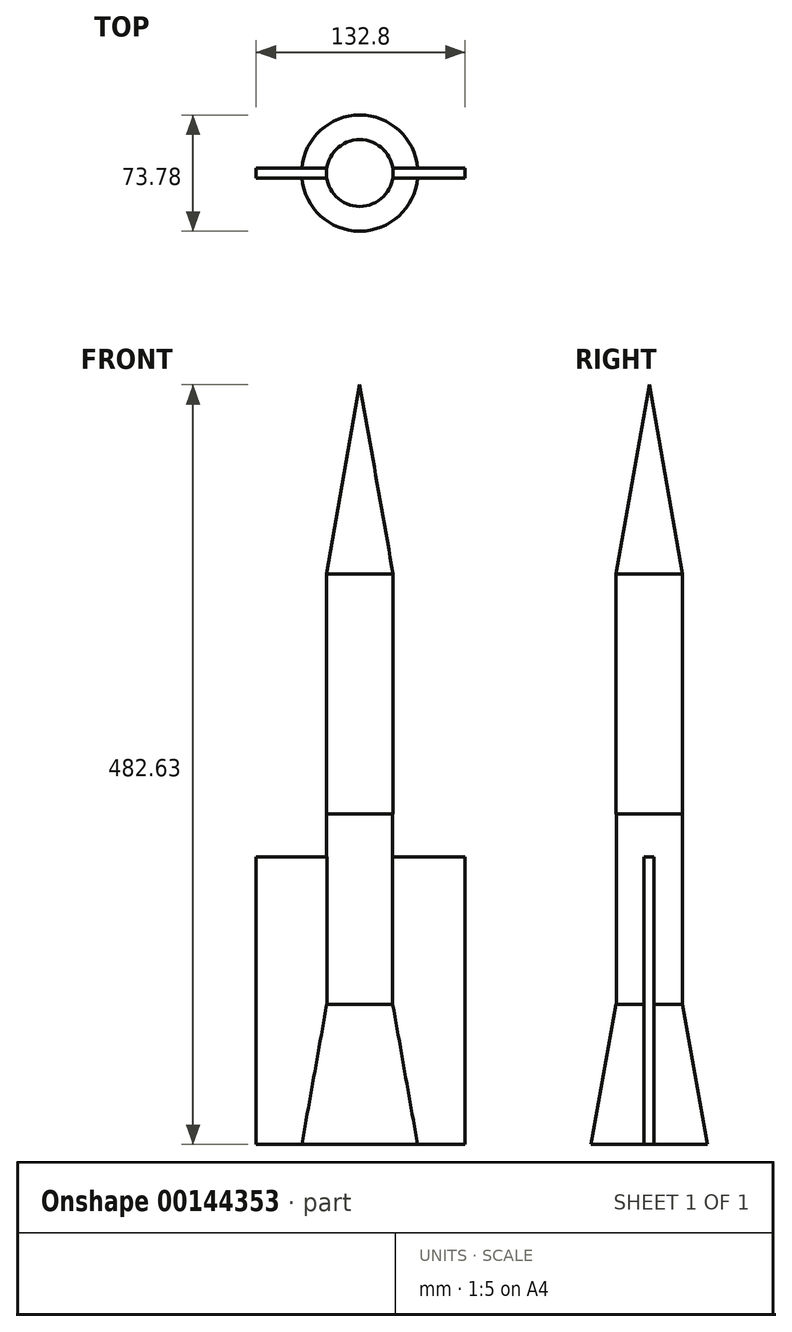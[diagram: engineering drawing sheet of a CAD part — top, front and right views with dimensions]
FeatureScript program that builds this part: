
annotation { "Feature Type Name" : "Feature", "Feature Type Description" : "" }
export const myFeature = defineFeature(function(context is Context, id is Id, definition is map)
    precondition{}
    {
        {
            var Q0;
            Q0=qCreatedBy(makeId("Top.planeOp"),FACE);
            var sketch = newSketch(context, id + "F0", { "sketchPlane" : qUnion([Q0])});
            skCircle(sketch, "E0", {"center": v(0, 0) * mm, "radius": 21.22 * mm});
            skSolve(sketch);
        }
        {
            var Q0;
            Q0=makeQuery(id+"F0.imprint","IMPRINT",FACE,{"disambiguationData":[TD([[makeQuery(id+"F0.imprint","IMPRINT",EDGE,{"derivedFrom":sQuery(id+"F0.wireOp",EDGE,"E0")}),1.0]])]});
            extrude(context, id + "F1", {"entities" : qUnion([Q0]), "depth" : 152.4 * mm});
        }
        {
            var Q0;
            Q0=makeQuery(id+"F1.opExtrude","CAP_FACE",FACE,{"disambiguationData":[OSD([sQuery(id+"F0.wireOp",EDGE,"E0")])],"isStart":false});
            var sketch = newSketch(context, id + "F2", { "sketchPlane" : qUnion([Q0])});
            skSolve(sketch);
        }
        {
            var Q0;
            Q0=makeQuery(id+"F2.imprint","IMPRINT",FACE,{"disambiguationData":[TD([[makeQuery(id+"F2.imprint","IMPRINT",EDGE,{"derivedFrom":makeQuery(id+"F1.opExtrude","CAP_EDGE",EDGE,{"disambiguationData":[OSD([sQuery(id+"F0.wireOp",EDGE,"E0")])],"isStart":false})}),1.0]])]});
            var sketch = newSketch(context, id + "F3", { "sketchPlane" : qUnion([Q0])});
            skSolve(sketch);
        }
        {
            var Q0;
            Q0=makeQuery(id+"F3.imprint","IMPRINT",FACE,{"disambiguationData":[TD([[makeQuery(id+"F3.imprint","IMPRINT",EDGE,{"derivedFrom":makeQuery(id+"F2.imprint","IMPRINT",EDGE,{"derivedFrom":makeQuery(id+"F1.opExtrude","CAP_EDGE",EDGE,{"disambiguationData":[OSD([sQuery(id+"F0.wireOp",EDGE,"E0")])],"isStart":false})})}),1.0]])]});
            var sketch = newSketch(context, id + "F4", { "sketchPlane" : qUnion([Q0])});
            skCircle(sketch, "E1.0", {"center": v(0, 0) * mm, "radius": 21.22 * mm});
            skSolve(sketch);
        }
        {
            var Q0;
            Q0 = qSketchRegion(id + "F4", true);
            extrude(context, id + "F5", {"entities" : qUnion([Q0]), "operationType" : NewBodyOperationType.ADD, "depth" : 2540 * mm, "hasDraft" : true, "draftAngle" : 10 * degree, "draftPullDirection" : true});
        }
        {
            var Q0;
            Q0=makeQuery(id+"F1.opExtrude","CAP_FACE",FACE,{"disambiguationData":[OSD([sQuery(id+"F0.wireOp",EDGE,"E0")])],"isStart":true});
            var sketch = newSketch(context, id + "F6", { "sketchPlane" : qUnion([Q0])});
            skCircle(sketch, "E2", {"center": v(0, 0) * mm, "radius": 20.95 * mm});
            skCircle(sketch, "E3", {"center": v(0, 0) * mm, "radius": 20.98 * mm});
            skSolve(sketch);
        }
        {
            var Q0;
            Q0=makeQuery(id+"F6.imprint","IMPRINT",FACE,{"disambiguationData":[TD([[makeQuery(id+"F6.imprint","IMPRINT",EDGE,{"derivedFrom":sQuery(id+"F6.wireOp",EDGE,"E2")}),1.0]])]});
            var Q1;
            Q1=sQuery(id+"F6.wireOp",EDGE,"E3");
            extrude(context, id + "F7", {"entities" : qUnion([Q0]), "operationType" : NewBodyOperationType.ADD, "surfaceEntities" : qUnion([Q1]), "depth" : 120.99 * mm});
        }
        {
            var Q0;
            Q0=makeQuery(id+"F7.opExtrude","CAP_FACE",FACE,{"disambiguationData":[OSD([sQuery(id+"F6.wireOp",EDGE,"E2")])],"isStart":false});
            var sketch = newSketch(context, id + "F8", { "sketchPlane" : qUnion([Q0])});
            skCircle(sketch, "E4.0", {"center": v(0, 0) * mm, "radius": 21.22 * mm});
            skSolve(sketch);
        }
        {
            var Q0;
            Q0=makeQuery(id+"F8.imprint","IMPRINT",FACE,{"disambiguationData":[TD([[makeQuery(id+"F8.imprint","IMPRINT",EDGE,{"derivedFrom":makeQuery(id+"F7.opExtrude","CAP_EDGE",EDGE,{"disambiguationData":[OSD([sQuery(id+"F6.wireOp",EDGE,"E2")])],"isStart":false})}),1.0]])]});
            var sketch = newSketch(context, id + "F9", { "sketchPlane" : qUnion([Q0])});
            skCircle(sketch, "E5.0", {"center": v(0, 0) * mm, "radius": 21.22 * mm});
            skSolve(sketch);
        }
        {
            var Q0;
            Q0 = qSketchRegion(id + "F9", true);
            extrude(context, id + "F10", {"entities" : qUnion([Q0]), "operationType" : NewBodyOperationType.ADD, "depth" : 88.9 * mm, "hasDraft" : true, "draftAngle" : 10 * degree});
        }
        {
            var Q0;
            Q0=makeQuery(id+"F10.opExtrude","CAP_FACE",FACE,{"disambiguationData":[OSD([sQuery(id+"F9.wireOp",EDGE,"E5.0")])],"isStart":false});
            var sketch = newSketch(context, id + "F11", { "sketchPlane" : qUnion([Q0])});
            skLineSegment(sketch, "E6.bottom", {"start": v(-65.8, 3.23) * mm, "end": v(66.99, 3.23) * mm});
            skLineSegment(sketch, "E6.top", {"start": v(-65.8, -3.04) * mm, "end": v(66.99, -3.04) * mm});
            skLineSegment(sketch, "E6.left", {"start": v(-65.8, 3.23) * mm, "end": v(-65.8, -3.04) * mm});
            skLineSegment(sketch, "E6.right", {"start": v(66.99, 3.23) * mm, "end": v(66.99, -3.04) * mm});
            skSolve(sketch);
        }
        {
            var Q0;
            Q0 = qSketchRegion(id + "F11", true);
            extrude(context, id + "F12", {"entities" : qUnion([Q0]), "operationType" : NewBodyOperationType.ADD, "oppositeDirection" : true, "depth" : 182.63 * mm});
        }
    });
